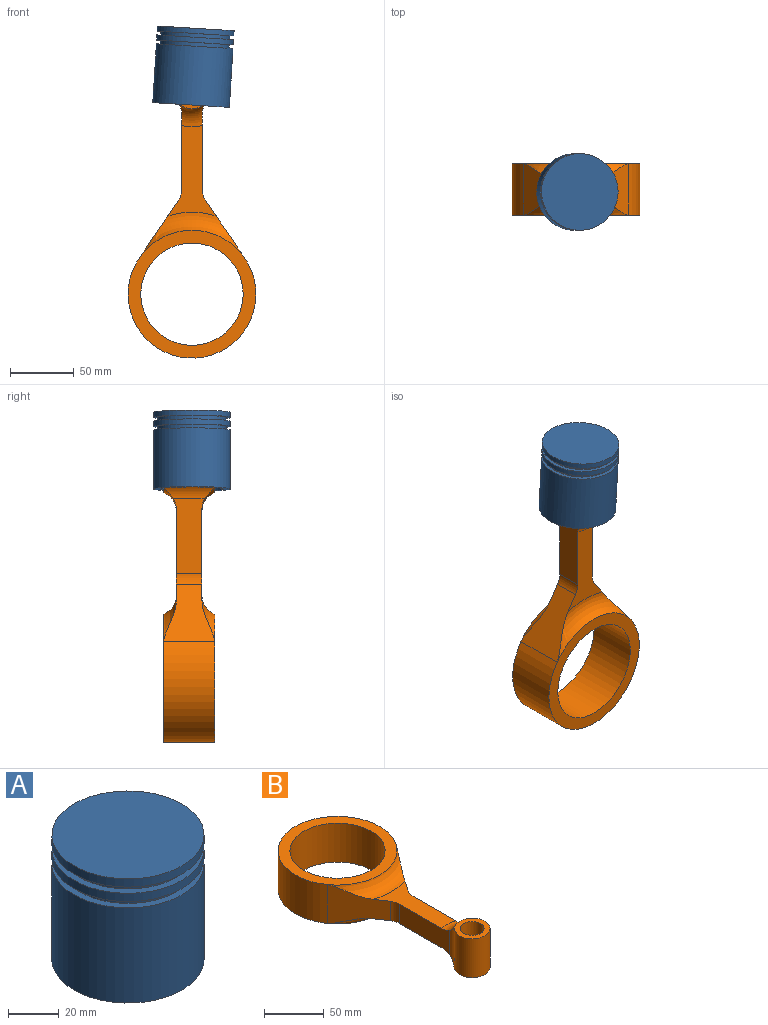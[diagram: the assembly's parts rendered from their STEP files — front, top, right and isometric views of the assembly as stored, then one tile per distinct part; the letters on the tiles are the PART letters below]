
ASSEMBLY  parts=2 mates=1
PART A: 14 faces, bbox 60x60x60 mm
  f0: cylinder r=25mm len=50mm, axis (0,0,-1), area 4856.1mm2, adj f1,f2,f13
  f1: plane 50x50mm, normal (0,0,-1), area 1963.5mm2, adj f0
  f2: plane 60x60mm, normal (0,0,-1), area 863.9mm2, adj f0,f3
  f3: cylinder r=30mm len=60mm, axis (0,0,-1), area 8670.8mm2, adj f2,f4
  f4: plane 60x60mm, normal (0,0,1), area 537.2mm2, adj f3,f5
  f5: cylinder r=27mm len=54mm, axis (0,0,-1), area 508.9mm2, adj f4,f6
  f6: plane 60x60mm, normal (0,0,-1), area 537.2mm2, adj f5,f7
  f7: cylinder r=30mm len=60mm, axis (0,0,-1), area 754mm2, adj f6,f8
  f8: plane 60x60mm, normal (0,0,1), area 537.2mm2, adj f7,f9
  f9: cylinder r=27mm len=54mm, axis (0,0,-1), area 508.9mm2, adj f8,f10
  f10: plane 60x60mm, normal (0,0,-1), area 537.2mm2, adj f9,f11
  f11: cylinder r=30mm len=60mm, axis (0,0,-1), area 754mm2, adj f10,f12
  f12: plane 60x60mm, normal (0,0,1), area 2827.4mm2, adj f11
  f13: cylinder r=10mm len=50mm, axis (-1,0,0), area 3012mm2, adj f0
PART B: 22 faces, bbox 132.4x225x50 mm
  f0: cylinder r=50mm len=100mm, axis (0,0,-1), area 8736.2mm2, adj f1,f6,f9,f18
  f1: plane 44.72x40mm, normal (-0.83,-0.56,0), area 1424.6mm2, adj f0,f8,f14,f15,f17,f21
  f2: plane 58.82x24.99mm, normal (-1,0,0), area 1190.7mm2, adj f8,f12,f13,f15,f17,f20
  f3: cylinder r=15mm len=40mm, axis (0,0,-1), area 2721.6mm2, adj f10,f11,f12,f19
  f4: plane 58.82x24.99mm, normal (1,0,0), area 1190.7mm2, adj f8,f11,f13,f16,f17,f20
  f5: cylinder r=10mm len=40mm, axis (0,0,-1), area 2513.3mm2, adj f10,f19
  f6: plane 44.72x40mm, normal (0.83,-0.56,0), area 1424.6mm2, adj f0,f8,f14,f16,f17,f21
  f7: cylinder r=40mm len=80mm, axis (0,0,-1), area 10053.1mm2, adj f9,f18
  f8: plane 70.67x37.68mm, normal (0,0,1), area 1224.8mm2, adj f1,f2,f4,f6,f13,f14,f15,f16
  f9: plane 100x100mm, normal (0,0,1), area 2827.4mm2, adj f0,f7,f14
  f10: plane 30x30mm, normal (0,0,1), area 392.7mm2, adj f3,f5,f13
  f11: cylinder r=15mm len=40mm, axis (0,0,-1), area 346.2mm2, adj f3,f4,f13,f20
  f12: cylinder r=15mm len=40mm, axis (0,0,-1), area 346.2mm2, adj f2,f3,f13,f20
  f13: torus R=29.14mm, axis (0,0,1), area 324.6mm2, adj f2,f4,f8,f10,f11,f12
  f14: torus R=64.14mm, axis (0,0,1), area 1112.4mm2, adj f1,f6,f8,f9
  f15: cylinder r=15mm len=20mm, axis (0,0,-1), area 178.7mm2, adj f1,f2,f8,f17
  f16: cylinder r=15mm len=20mm, axis (0,0,1), area 178.7mm2, adj f4,f6,f8,f17
  f17: plane 70.67x37.68mm, normal (0,0,-1), area 1224.8mm2, adj f1,f2,f4,f6,f15,f16,f20,f21
  f18: plane 100x100mm, normal (0,0,-1), area 2827.4mm2, adj f0,f7,f21
  f19: plane 30x30mm, normal (0,0,-1), area 392.7mm2, adj f3,f5,f20
  f20: torus R=29.14mm, axis (0,0,-1), area 324.6mm2, adj f2,f4,f11,f12,f17,f19
  f21: torus R=64.14mm, axis (0,0,-1), area 1112.4mm2, adj f1,f6,f17,f18
PLACE A rot(axis=(0.03,0.03,1),90.1deg) t=(-5.51,-36.13,20.95)mm
PLACE B rot(axis=(-1,0,0),90deg) t=(-4.76,-33.91,32.93)mm fixed
MATE cylindrical A.f13 <-> B.f5  axis (0,-1,0) through (-4.76,-36.13,32.93)mm
